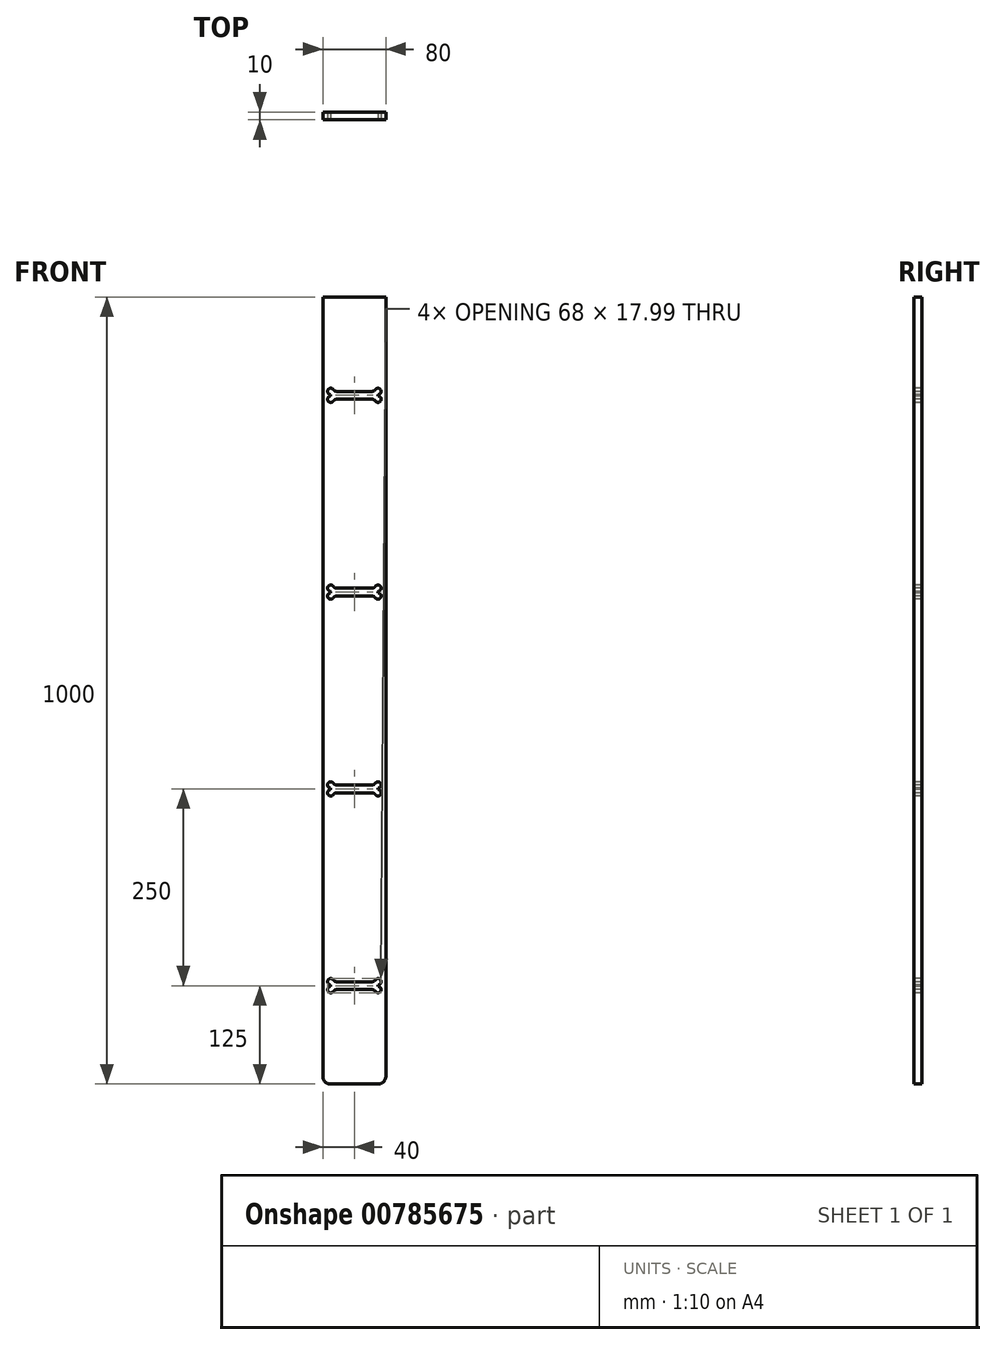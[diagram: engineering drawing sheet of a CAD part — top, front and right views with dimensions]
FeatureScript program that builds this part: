
annotation { "Feature Type Name" : "Feature", "Feature Type Description" : "" }
export const myFeature = defineFeature(function(context is Context, id is Id, definition is map)
    precondition{}
    {
        {
            assignVariable(context, id + "F0", {"name" : "PlywoodThick", "anyValue" : 10});
        }
        {
            var Q0;
            Q0=qCreatedBy(makeId("Front.planeOp"),FACE);
            var sketch = newSketch(context, id + "F1", { "sketchPlane" : qUnion([Q0])});
            skLineSegment(sketch, "E0.bottom", {"start": v(40, -500) * mm, "end": v(-40, -500) * mm});
            skLineSegment(sketch, "E0.top", {"start": v(40, 500) * mm, "end": v(-40, 500) * mm});
            skLineSegment(sketch, "E0.left", {"start": v(40, -500) * mm, "end": v(40, 500) * mm});
            skLineSegment(sketch, "E0.right", {"start": v(-40, -500) * mm, "end": v(-40, 500) * mm});
            skPoint(sketch, "E0.middle", {"position": v(0, 0) * mm});
            skSolve(sketch);
        }
        {
            var Q0;
            Q0 = qSketchRegion(id + "F1", true);
            extrude(context, id + "F2", {"entities" : qUnion([Q0]), "depth" : (getVariable(context, 'PlywoodThick')) * mm, "offsetDistance" : 25 * mm});
        }
        {
            var Q0;
            Q0=makeQuery(id+"F2.opExtrude","SWEPT_EDGE",EDGE,{"disambiguationData":[OSD([sQuery(id+"F1.wireOp",EDGE,"E0.bottom"),sQuery(id+"F1.wireOp",EDGE,"E0.left")])]});
            var Q1;
            Q1=makeQuery(id+"F2.opExtrude","SWEPT_EDGE",EDGE,{"disambiguationData":[OSD([sQuery(id+"F1.wireOp",EDGE,"E0.bottom"),sQuery(id+"F1.wireOp",EDGE,"E0.right")])]});
            fillet(context, id + "F3", {"entities" : qUnion([Q0, Q1]), "radius" : 10 * mm, "tangentPropagation" : true, "allowEdgeOverflow" : false});
        }
        {
            var Q0;
            Q0=makeQuery(id+"F2.opExtrude","CAP_FACE",FACE,{"disambiguationData":[OSD([sQuery(id+"F1.wireOp",EDGE,"E0.bottom"),sQuery(id+"F1.wireOp",EDGE,"E0.top"),sQuery(id+"F1.wireOp",EDGE,"E0.left"),sQuery(id+"F1.wireOp",EDGE,"E0.right")])],"isStart":false});
            var sketch = newSketch(context, id + "F4", { "sketchPlane" : qUnion([Q0])});
            skLineSegment(sketch, "E1", {"start": v(0, 500) * mm, "end": v(0, -500) * mm, "construction": true});
            skLineSegment(sketch, "E2.bottom", {"start": v(22.52, -380) * mm, "end": v(-22.52, -380) * mm});
            skLineSegment(sketch, "E2.top", {"start": v(22.52, -370) * mm, "end": v(-22.52, -370) * mm});
            skLineSegment(sketch, "E2.left", {"start": v(30, -376) * mm, "end": v(30, -374) * mm});
            skLineSegment(sketch, "E2.right", {"start": v(-30, -376) * mm, "end": v(-30, -374) * mm});
            skPoint(sketch, "E2.middle", {"position": v(0, -375) * mm});
            skPoint(sketch, "E3.0.1.4", {"position": v(0, -205) * mm});
            skPoint(sketch, "E3.0.2.4", {"position": v(0, 45) * mm});
            skPoint(sketch, "E3.0.3.4", {"position": v(0, 295) * mm});
            skLineSegment(sketch, "E3.direction1", {"start": v(-22.52, -370) * mm, "end": v(22.52, -370) * mm, "construction": true});
            skArc(sketch, "E4", {"start": v(26.67, -382.22) * mm, "mid": v(33.53, -381.89) * mm, "end": v(30, -376) * mm});
            skArc(sketch, "E5", {"start": v(30, -374) * mm, "mid": v(33.53, -368.11) * mm, "end": v(26.67, -367.78) * mm});
            skArc(sketch, "E6", {"start": v(-30, -376) * mm, "mid": v(-33.53, -381.89) * mm, "end": v(-26.67, -382.22) * mm});
            skArc(sketch, "E7", {"start": v(-26.67, -367.78) * mm, "mid": v(-33.53, -368.11) * mm, "end": v(-30, -374) * mm});
            skPoint(sketch, "E8.visualSharp", {"position": v(-26, -380) * mm});
            skArc(sketch, "E8.filletArc", {"start": v(-22.52, -380) * mm, "mid": v(-24.87, -380.6) * mm, "end": v(-26.67, -382.22) * mm});
            skPoint(sketch, "E9.visualSharp", {"position": v(-26, -370) * mm});
            skArc(sketch, "E9.filletArc", {"start": v(-26.67, -367.78) * mm, "mid": v(-24.87, -369.4) * mm, "end": v(-22.52, -370) * mm});
            skPoint(sketch, "E10.visualSharp", {"position": v(26, -380) * mm});
            skArc(sketch, "E10.filletArc", {"start": v(26.67, -382.22) * mm, "mid": v(24.87, -380.6) * mm, "end": v(22.52, -380) * mm});
            skPoint(sketch, "E11.visualSharp", {"position": v(26, -370) * mm});
            skArc(sketch, "E11.filletArc", {"start": v(22.52, -370) * mm, "mid": v(24.87, -369.4) * mm, "end": v(26.67, -367.78) * mm});
            skPoint(sketch, "E12.0.1.0", {"position": v(0, -125) * mm});
            skArc(sketch, "E12.0.1.1", {"start": v(30, -124) * mm, "mid": v(33.53, -118.11) * mm, "end": v(26.67, -117.78) * mm});
            skPoint(sketch, "E12.0.1.2", {"position": v(26, -120) * mm});
            skPoint(sketch, "E12.0.1.3", {"position": v(-26, -120) * mm});
            skLineSegment(sketch, "E12.0.1.4", {"start": v(-22.52, -120) * mm, "end": v(22.52, -120) * mm, "construction": true});
            skArc(sketch, "E12.0.1.5", {"start": v(-26.67, -117.78) * mm, "mid": v(-33.53, -118.11) * mm, "end": v(-30, -124) * mm});
            skLineSegment(sketch, "E12.0.1.6", {"start": v(22.52, -130) * mm, "end": v(-22.52, -130) * mm});
            skArc(sketch, "E12.0.1.7", {"start": v(-30, -126) * mm, "mid": v(-33.53, -131.89) * mm, "end": v(-26.67, -132.22) * mm});
            skPoint(sketch, "E12.0.1.8", {"position": v(-26, -130) * mm});
            skPoint(sketch, "E12.0.1.9", {"position": v(26, -130) * mm});
            skArc(sketch, "E12.0.1.10", {"start": v(26.67, -132.22) * mm, "mid": v(33.53, -131.89) * mm, "end": v(30, -126) * mm});
            skArc(sketch, "E12.0.1.11", {"start": v(26.67, -132.22) * mm, "mid": v(24.87, -130.6) * mm, "end": v(22.52, -130) * mm});
            skArc(sketch, "E12.0.1.12", {"start": v(22.52, -120) * mm, "mid": v(24.87, -119.4) * mm, "end": v(26.67, -117.78) * mm});
            skArc(sketch, "E12.0.1.13", {"start": v(-22.52, -130) * mm, "mid": v(-24.87, -130.6) * mm, "end": v(-26.67, -132.22) * mm});
            skArc(sketch, "E12.0.1.14", {"start": v(-26.67, -117.78) * mm, "mid": v(-24.87, -119.4) * mm, "end": v(-22.52, -120) * mm});
            skLineSegment(sketch, "E12.0.1.15", {"start": v(22.52, -120) * mm, "end": v(-22.52, -120) * mm});
            skLineSegment(sketch, "E12.0.1.16", {"start": v(30, -126) * mm, "end": v(30, -124) * mm});
            skLineSegment(sketch, "E12.0.1.17", {"start": v(-30, -126) * mm, "end": v(-30, -124) * mm});
            skPoint(sketch, "E12.0.2.0", {"position": v(0, 125) * mm});
            skArc(sketch, "E12.0.2.1", {"start": v(30, 126) * mm, "mid": v(33.53, 131.89) * mm, "end": v(26.67, 132.22) * mm});
            skPoint(sketch, "E12.0.2.2", {"position": v(26, 130) * mm});
            skPoint(sketch, "E12.0.2.3", {"position": v(-26, 130) * mm});
            skLineSegment(sketch, "E12.0.2.4", {"start": v(-22.52, 130) * mm, "end": v(22.52, 130) * mm, "construction": true});
            skArc(sketch, "E12.0.2.5", {"start": v(-26.67, 132.22) * mm, "mid": v(-33.53, 131.89) * mm, "end": v(-30, 126) * mm});
            skLineSegment(sketch, "E12.0.2.6", {"start": v(22.52, 120) * mm, "end": v(-22.52, 120) * mm});
            skArc(sketch, "E12.0.2.7", {"start": v(-30, 124) * mm, "mid": v(-33.53, 118.11) * mm, "end": v(-26.67, 117.78) * mm});
            skPoint(sketch, "E12.0.2.8", {"position": v(-26, 120) * mm});
            skPoint(sketch, "E12.0.2.9", {"position": v(26, 120) * mm});
            skArc(sketch, "E12.0.2.10", {"start": v(26.67, 117.78) * mm, "mid": v(33.53, 118.11) * mm, "end": v(30, 124) * mm});
            skArc(sketch, "E12.0.2.11", {"start": v(26.67, 117.78) * mm, "mid": v(24.87, 119.4) * mm, "end": v(22.52, 120) * mm});
            skArc(sketch, "E12.0.2.12", {"start": v(22.52, 130) * mm, "mid": v(24.87, 130.6) * mm, "end": v(26.67, 132.22) * mm});
            skArc(sketch, "E12.0.2.13", {"start": v(-22.52, 120) * mm, "mid": v(-24.87, 119.4) * mm, "end": v(-26.67, 117.78) * mm});
            skArc(sketch, "E12.0.2.14", {"start": v(-26.67, 132.22) * mm, "mid": v(-24.87, 130.6) * mm, "end": v(-22.52, 130) * mm});
            skLineSegment(sketch, "E12.0.2.15", {"start": v(22.52, 130) * mm, "end": v(-22.52, 130) * mm});
            skLineSegment(sketch, "E12.0.2.16", {"start": v(30, 124) * mm, "end": v(30, 126) * mm});
            skLineSegment(sketch, "E12.0.2.17", {"start": v(-30, 124) * mm, "end": v(-30, 126) * mm});
            skPoint(sketch, "E12.0.3.0", {"position": v(0, 375) * mm});
            skArc(sketch, "E12.0.3.1", {"start": v(30, 376) * mm, "mid": v(33.53, 381.89) * mm, "end": v(26.67, 382.22) * mm});
            skPoint(sketch, "E12.0.3.2", {"position": v(26, 380) * mm});
            skPoint(sketch, "E12.0.3.3", {"position": v(-26, 380) * mm});
            skLineSegment(sketch, "E12.0.3.4", {"start": v(-22.52, 380) * mm, "end": v(22.52, 380) * mm, "construction": true});
            skArc(sketch, "E12.0.3.5", {"start": v(-26.67, 382.22) * mm, "mid": v(-33.53, 381.89) * mm, "end": v(-30, 376) * mm});
            skLineSegment(sketch, "E12.0.3.6", {"start": v(22.52, 370) * mm, "end": v(-22.52, 370) * mm});
            skArc(sketch, "E12.0.3.7", {"start": v(-30, 374) * mm, "mid": v(-33.53, 368.11) * mm, "end": v(-26.67, 367.78) * mm});
            skPoint(sketch, "E12.0.3.8", {"position": v(-26, 370) * mm});
            skPoint(sketch, "E12.0.3.9", {"position": v(26, 370) * mm});
            skArc(sketch, "E12.0.3.10", {"start": v(26.67, 367.78) * mm, "mid": v(33.53, 368.11) * mm, "end": v(30, 374) * mm});
            skArc(sketch, "E12.0.3.11", {"start": v(26.67, 367.78) * mm, "mid": v(24.87, 369.4) * mm, "end": v(22.52, 370) * mm});
            skArc(sketch, "E12.0.3.12", {"start": v(22.52, 380) * mm, "mid": v(24.87, 380.6) * mm, "end": v(26.67, 382.22) * mm});
            skArc(sketch, "E12.0.3.13", {"start": v(-22.52, 370) * mm, "mid": v(-24.87, 369.4) * mm, "end": v(-26.67, 367.78) * mm});
            skArc(sketch, "E12.0.3.14", {"start": v(-26.67, 382.22) * mm, "mid": v(-24.87, 380.6) * mm, "end": v(-22.52, 380) * mm});
            skLineSegment(sketch, "E12.0.3.15", {"start": v(22.52, 380) * mm, "end": v(-22.52, 380) * mm});
            skLineSegment(sketch, "E12.0.3.16", {"start": v(30, 374) * mm, "end": v(30, 376) * mm});
            skLineSegment(sketch, "E12.0.3.17", {"start": v(-30, 374) * mm, "end": v(-30, 376) * mm});
            skLineSegment(sketch, "E12.direction1", {"start": v(-30, -380) * mm, "end": v(-5, -380) * mm, "construction": true});
            skLineSegment(sketch, "E12.direction2", {"start": v(-30, -380) * mm, "end": v(-30, -130) * mm, "construction": true});
            skSolve(sketch);
        }
        {
            var Q0;
            Q0=makeQuery(id+"F4.imprint","IMPRINT",FACE,{"disambiguationData":[TD([[makeQuery(id+"F4.imprint","IMPRINT",EDGE,{"derivedFrom":sQuery(id+"F4.wireOp",EDGE,"E2.bottom")}),-1.0]])]});
            var Q1;
            Q1=makeQuery(id+"F4.imprint","IMPRINT",FACE,{"disambiguationData":[TD([[makeQuery(id+"F4.imprint","IMPRINT",EDGE,{"derivedFrom":sQuery(id+"F4.wireOp",EDGE,"E12.0.1.1")}),1.0]])]});
            var Q2;
            Q2=makeQuery(id+"F4.imprint","IMPRINT",FACE,{"disambiguationData":[TD([[makeQuery(id+"F4.imprint","IMPRINT",EDGE,{"derivedFrom":sQuery(id+"F4.wireOp",EDGE,"E12.0.2.1")}),1.0]])]});
            var Q3;
            Q3=makeQuery(id+"F4.imprint","IMPRINT",FACE,{"disambiguationData":[TD([[makeQuery(id+"F4.imprint","IMPRINT",EDGE,{"derivedFrom":sQuery(id+"F4.wireOp",EDGE,"E12.0.3.1")}),1.0]])]});
            extrude(context, id + "F5", {"entities" : qUnion([Q0, Q1, Q2, Q3]), "operationType" : NewBodyOperationType.REMOVE, "endBound" : BoundingType.THROUGH_ALL, "oppositeDirection" : true, "depth" : 25 * mm, "offsetDistance" : 25 * mm});
        }
    });
